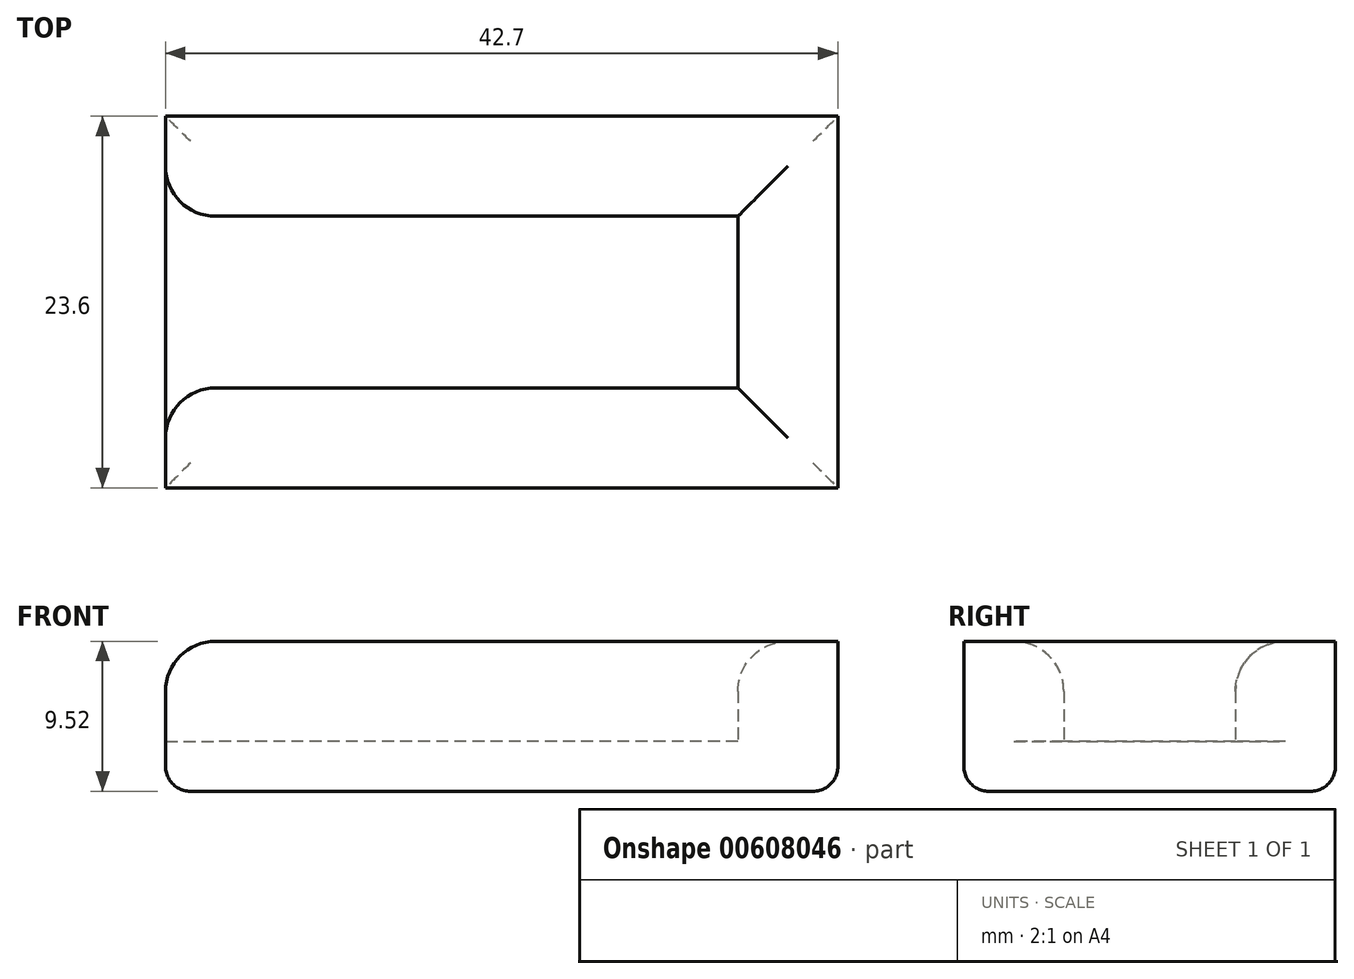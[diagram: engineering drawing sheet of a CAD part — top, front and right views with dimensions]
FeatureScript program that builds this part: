
annotation { "Feature Type Name" : "Feature", "Feature Type Description" : "" }
export const myFeature = defineFeature(function(context is Context, id is Id, definition is map)
    precondition{}
    {
        {
            var Q0;
            Q0=qCreatedBy(makeId("Top.planeOp"),FACE);
            var sketch = newSketch(context, id + "F0", { "sketchPlane" : qUnion([Q0])});
            skLineSegment(sketch, "E0.bottom", {"start": v(15, 5.45) * mm, "end": v(-15, 5.45) * mm});
            skLineSegment(sketch, "E0.top", {"start": v(15, -5.45) * mm, "end": v(-15, -5.45) * mm});
            skLineSegment(sketch, "E0.left", {"start": v(15, 5.45) * mm, "end": v(15, -5.45) * mm});
            skLineSegment(sketch, "E0.right", {"start": v(-15, 5.45) * mm, "end": v(-15, -5.45) * mm});
            skPoint(sketch, "E0.middle", {"position": v(0, 0) * mm});
            skLineSegment(sketch, "E1.bottom", {"start": v(-21.35, -11.8) * mm, "end": v(21.35, -11.8) * mm});
            skLineSegment(sketch, "E1.top", {"start": v(-21.35, 11.8) * mm, "end": v(21.35, 11.8) * mm});
            skLineSegment(sketch, "E1.left", {"start": v(-21.35, -11.8) * mm, "end": v(-21.35, 11.8) * mm});
            skLineSegment(sketch, "E1.right", {"start": v(21.35, -11.8) * mm, "end": v(21.35, 11.8) * mm});
            skLineSegment(sketch, "E2", {"start": v(-15, 5.45) * mm, "end": v(-21.35, 5.45) * mm});
            skLineSegment(sketch, "E3", {"start": v(-15, -5.45) * mm, "end": v(-21.35, -5.45) * mm});
            skSolve(sketch);
        }
        {
            var Q0;
            Q0=makeQuery(id+"F0.imprint","IMPRINT",FACE,{"disambiguationData":[TD([[makeQuery(id+"F0.imprint","IMPRINT",EDGE,{"derivedFrom":sQuery(id+"F0.wireOp",EDGE,"E0.bottom")}),-1.0]])]});
            var Q1;
            Q1=makeQuery(id+"F0.imprint","IMPRINT",FACE,{"disambiguationData":[TD([[makeQuery(id+"F0.imprint","IMPRINT",EDGE,{"derivedFrom":sQuery(id+"F0.wireOp",EDGE,"E0.bottom")}),1.0]])]});
            var Q2;
            Q2=makeQuery(id+"F0.imprint","IMPRINT",FACE,{"disambiguationData":[TD([[makeQuery(id+"F0.imprint","IMPRINT",EDGE,{"derivedFrom":sQuery(id+"F0.wireOp",EDGE,"E0.right")}),-1.0]])]});
            extrude(context, id + "F1", {"entities" : qUnion([Q0, Q1, Q2]), "oppositeDirection" : true, "depth" : 3.17 * mm, "offsetDistance" : 25.4 * mm});
        }
        {
            var Q0;
            Q0=makeQuery(id+"F0.imprint","IMPRINT",FACE,{"disambiguationData":[TD([[makeQuery(id+"F0.imprint","IMPRINT",EDGE,{"derivedFrom":sQuery(id+"F0.wireOp",EDGE,"E0.bottom")}),-1.0]])]});
            extrude(context, id + "F2", {"entities" : qUnion([Q0]), "operationType" : NewBodyOperationType.ADD, "depth" : 6.35 * mm, "offsetDistance" : 25.4 * mm});
        }
        {
            var Q0;
            Q0=makeQuery(id+"F2.opExtrude","SWEPT_EDGE",EDGE,{"disambiguationData":[OSD([sQuery(id+"F0.wireOp",EDGE,"E1.left"),sQuery(id+"F0.wireOp",EDGE,"E2")])]});
            var Q1;
            Q1=makeQuery(id+"F2.opExtrude","SWEPT_EDGE",EDGE,{"disambiguationData":[OSD([sQuery(id+"F0.wireOp",EDGE,"E1.left"),sQuery(id+"F0.wireOp",EDGE,"E3")])]});
            fillet(context, id + "F3", {"entities" : qUnion([Q0, Q1]), "radius" : 3.17 * mm, "tangentPropagation" : true, "allowEdgeOverflow" : false});
        }
        {
            var Q0;
            Q0=makeQuery(id+"F2.opExtrude","CAP_EDGE",EDGE,{"disambiguationData":[OSD([sQuery(id+"F0.wireOp",EDGE,"E0.bottom"),sQuery(id+"F0.wireOp",EDGE,"E2")])],"isStart":false});
            var Q1;
            Q1=makeQuery(id+"F2.opExtrude","CAP_EDGE",EDGE,{"disambiguationData":[OSD([sQuery(id+"F0.wireOp",EDGE,"E0.top"),sQuery(id+"F0.wireOp",EDGE,"E3")])],"isStart":false});
            var Q2;
            Q2=makeQuery(id+"F2.opExtrude","CAP_EDGE",EDGE,{"disambiguationData":[OSD([sQuery(id+"F0.wireOp",EDGE,"E0.left")])],"isStart":false});
            fillet(context, id + "F4", {"entities" : qUnion([Q0, Q1, Q2]), "radius" : 3.17 * mm, "tangentPropagation" : true, "allowEdgeOverflow" : false});
        }
        {
            var Q0;
            Q0=makeQuery(id+"F1.opExtrude","CAP_FACE",FACE,{"disambiguationData":[OSD([sQuery(id+"F0.wireOp",EDGE,"E1.bottom"),sQuery(id+"F0.wireOp",EDGE,"E1.top"),sQuery(id+"F0.wireOp",EDGE,"E1.left"),sQuery(id+"F0.wireOp",EDGE,"E1.right")])],"isStart":false});
            fillet(context, id + "F5", {"entities" : qUnion([Q0]), "radius" : 1.59 * mm, "tangentPropagation" : true, "allowEdgeOverflow" : false});
        }
    });
